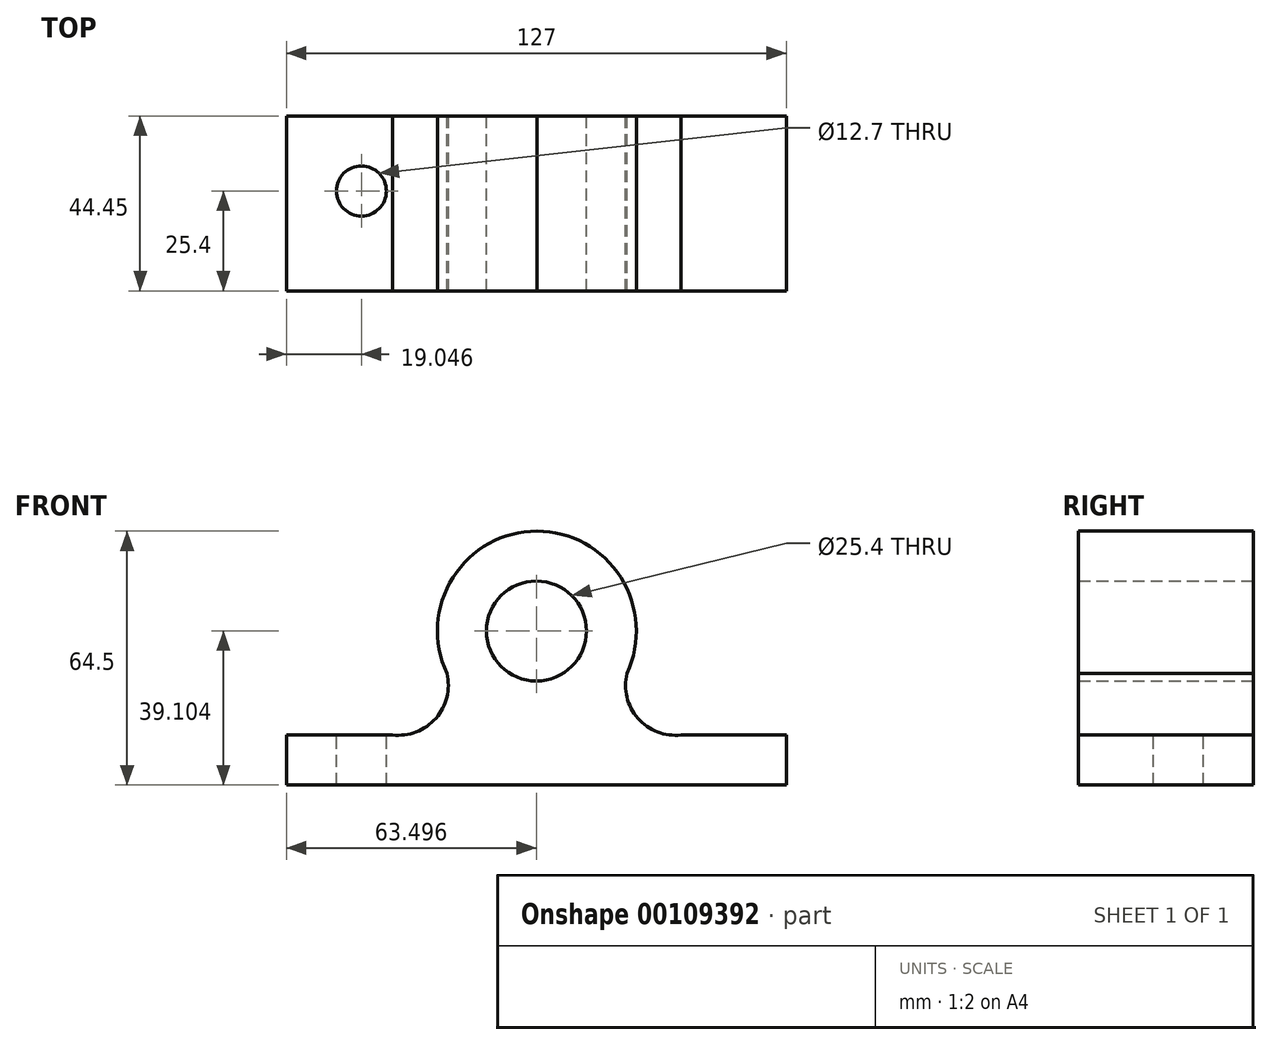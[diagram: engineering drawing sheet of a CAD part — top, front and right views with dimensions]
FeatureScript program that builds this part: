
annotation { "Feature Type Name" : "Feature", "Feature Type Description" : "" }
export const myFeature = defineFeature(function(context is Context, id is Id, definition is map)
    precondition{}
    {
        {
            var Q0;
            Q0=qCreatedBy(makeId("Front.planeOp"),FACE);
            var sketch = newSketch(context, id + "F0", { "sketchPlane" : qUnion([Q0])});
            skArc(sketch, "E0", {"start": v(43.96, 32.46) * mm, "mid": v(42.4, 56.79) * mm, "end": v(21.08, 68.6) * mm});
            skArc(sketch, "E1", {"start": v(43.96, 32.46) * mm, "mid": v(46.76, 21.02) * mm, "end": v(57.75, 16.8) * mm});
            skLineSegment(sketch, "E2", {"start": v(-42.55, 16.8) * mm, "end": v(-42.55, 4.1) * mm});
            skLineSegment(sketch, "E3", {"start": v(-42.55, 4.1) * mm, "end": v(84.45, 4.1) * mm});
            skLineSegment(sketch, "E4", {"start": v(84.45, 4.1) * mm, "end": v(84.45, 16.8) * mm});
            skLineSegment(sketch, "E5", {"start": v(84.45, 16.8) * mm, "end": v(57.75, 16.8) * mm});
            skCircle(sketch, "E6", {"center": v(20.95, 43.2) * mm, "radius": 12.7 * mm});
            skArc(sketch, "E7.MirrorCS", {"start": v(-1.8, 32.46) * mm, "mid": v(-4.59, 21.02) * mm, "end": v(-15.58, 16.8) * mm});
            skLineSegment(sketch, "E8.MirrorCS", {"start": v(-42.28, 16.8) * mm, "end": v(-15.58, 16.8) * mm});
            skArc(sketch, "E9.MirrorCS", {"start": v(-1.8, 32.46) * mm, "mid": v(-0.24, 56.79) * mm, "end": v(21.08, 68.6) * mm});
            skLineSegment(sketch, "E10", {"start": v(-42.28, 16.8) * mm, "end": v(-42.55, 16.8) * mm});
            skSolve(sketch);
        }
        {
            var Q0;
            Q0=makeQuery(id+"F0.imprint","IMPRINT",FACE,{"disambiguationData":[TD([[makeQuery(id+"F0.imprint","IMPRINT",EDGE,{"derivedFrom":sQuery(id+"F0.wireOp",EDGE,"E0")}),1.0]])]});
            extrude(context, id + "F1", {"entities" : qUnion([Q0]), "depth" : 44.45 * mm});
        }
        {
            var Q0;
            Q0=makeQuery(id+"F1.opExtrude","SWEPT_FACE",FACE,{"disambiguationData":[OSD([sQuery(id+"F0.wireOp",EDGE,"E8.MirrorCS"),sQuery(id+"F0.wireOp",EDGE,"E10")])]});
            var sketch = newSketch(context, id + "F2", { "sketchPlane" : qUnion([Q0])});
            skPoint(sketch, "E11.positionSnap0", {"position": v(-15.58, -22.23) * mm});
            skCircle(sketch, "E12", {"center": v(-23.5, -19.05) * mm, "radius": 6.35 * mm});
            skLineSegment(sketch, "E13", {"start": v(21.17, -46.02) * mm, "end": v(21.17, 5.67) * mm, "construction": true});
            skCircle(sketch, "E14.MirrorC", {"center": v(65.83, -19.05) * mm, "radius": 6.35 * mm});
            skSolve(sketch);
        }
        {
            var Q0;
            Q0=makeQuery(id+"F2.imprint","IMPRINT",FACE,{"disambiguationData":[TD([[makeQuery(id+"F2.imprint","IMPRINT",EDGE,{"derivedFrom":sQuery(id+"F2.wireOp",EDGE,"E14.MirrorC")}),-1.0]])]});
            var Q1;
            Q1=makeQuery(id+"F2.imprint","IMPRINT",FACE,{"disambiguationData":[TD([[makeQuery(id+"F2.imprint","IMPRINT",EDGE,{"derivedFrom":sQuery(id+"F2.wireOp",EDGE,"E12")}),1.0]])]});
            extrude(context, id + "F3", {"entities" : qUnion([Q0, Q1]), "operationType" : NewBodyOperationType.REMOVE, "endBound" : BoundingType.THROUGH_ALL, "oppositeDirection" : true, "depth" : 25.4 * mm});
        }
    });
